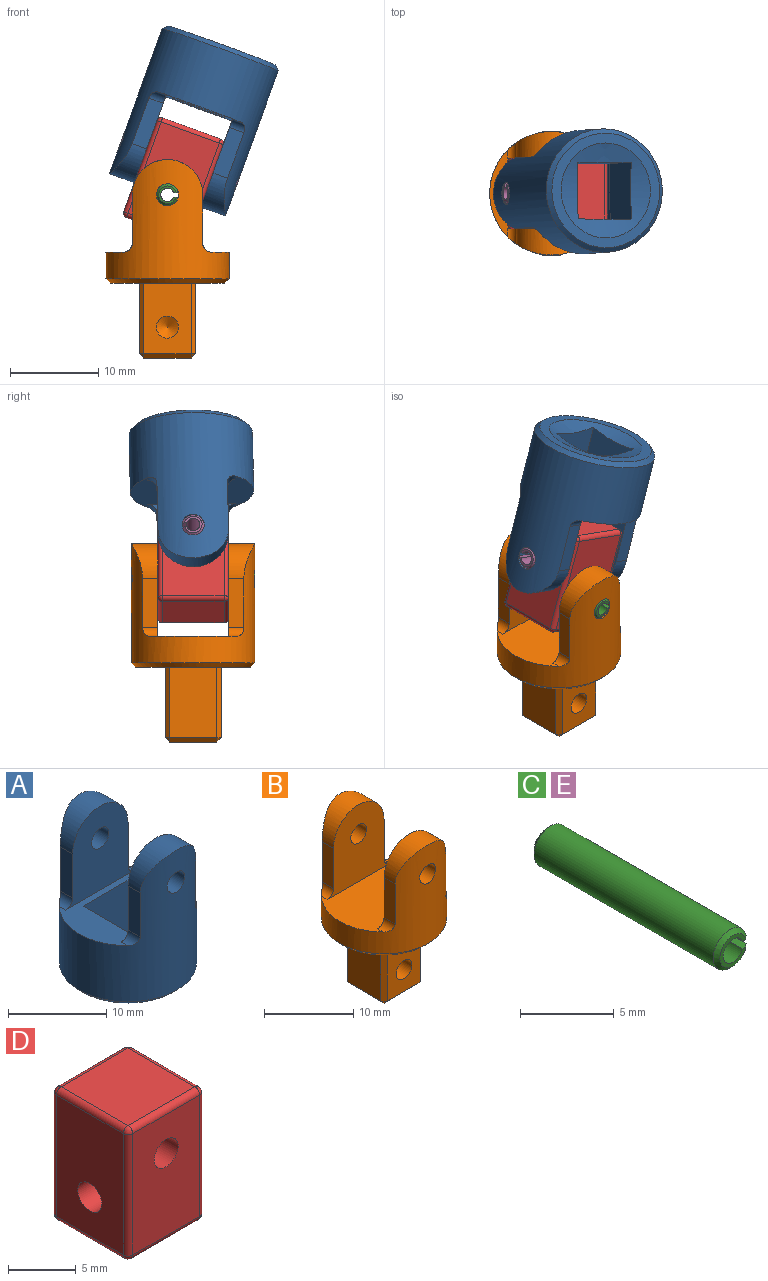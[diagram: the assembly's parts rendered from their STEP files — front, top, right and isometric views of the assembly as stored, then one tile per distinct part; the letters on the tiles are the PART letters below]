
ASSEMBLY  parts=5 mates=4
PART A: 23 faces, bbox 14x14x18 mm
  f0: plane 13x13mm, normal (0,0,-1), area 41.6mm2, adj f21,f22
  f1: plane 14x9.8mm, normal (0,0,1), area 65.4mm2, adj f3,f6,f8,f10,f13,f15,f16,f17
  f2: cylinder r=4mm len=8mm, axis (0,1,0), area 30mm2, adj f4,f5,f8,f16
  f3: cylinder r=1mm len=1.74mm, axis (0,1,0), area 2.3mm2, adj f1,f4,f8,f16
  f4: plane 5.5x1.74mm, normal (-1,0,0), area 9.6mm2, adj f2,f3,f8,f16
  f5: plane 5.5x1.74mm, normal (1,0,0), area 9.6mm2, adj f2,f6,f8,f16
  f6: cylinder r=1mm len=1.74mm, axis (0,1,0), area 2.3mm2, adj f1,f5,f8,f16
  f7: cylinder r=1.25mm len=3mm, axis (0,1,0), area 23.1mm2, adj f8,f16
  f8: cylinder r=7mm len=17.5mm, axis (0,0,-1), area 462.4mm2, adj f1,f2,f3,f4,f5,f6,f7,f9
  f9: cylinder r=4mm len=8mm, axis (0,1,0), area 30mm2, adj f8,f11,f12,f15
  f10: cylinder r=1mm len=1.74mm, axis (0,1,0), area 2.3mm2, adj f1,f8,f11,f15
  f11: plane 5.5x1.74mm, normal (-1,0,0), area 9.6mm2, adj f8,f9,f10,f15
  f12: plane 5.5x1.74mm, normal (1,0,0), area 9.6mm2, adj f8,f9,f13,f15
  f13: cylinder r=1mm len=1.74mm, axis (0,1,0), area 2.3mm2, adj f1,f8,f12,f15
  f14: cylinder r=1.25mm len=3mm, axis (0,1,0), area 23.1mm2, adj f8,f15
  f15: plane 10.5x10mm, normal (0,-1,0), area 72.7mm2, adj f1,f9,f10,f11,f12,f13,f14
  f16: plane 10.5x10mm, normal (0,1,0), area 72.7mm2, adj f1,f2,f3,f4,f5,f6,f7
  f17: plane 7.21x6.45mm, normal (-1,0,0), area 45mm2, adj f1,f18,f20,f22
  f18: plane 7.21x6.45mm, normal (0,-1,0), area 45mm2, adj f1,f17,f19,f22
  f19: plane 7.21x6.45mm, normal (1,0,0), area 45mm2, adj f1,f18,f20,f22
  f20: plane 7.21x6.45mm, normal (0,1,0), area 45mm2, adj f1,f17,f19,f22
  f21: cone r=7mm half-angle=45deg, axis (0,0,1), area 30mm2, adj f0,f8
  f22: sphere r=15mm, area 52mm2, adj f0,f17,f18,f19,f20
PART B: 37 faces, bbox 14x14x22.5 mm
  f0: cylinder r=4mm len=8mm, axis (0,1,0), area 30mm2, adj f2,f3,f6,f16
  f1: cylinder r=1mm len=1.74mm, axis (0,1,0), area 2.3mm2, adj f2,f6,f9,f16
  f2: plane 5.5x1.74mm, normal (-1,0,0), area 9.6mm2, adj f0,f1,f6,f16
  f3: plane 5.5x1.74mm, normal (1,0,0), area 9.6mm2, adj f0,f4,f6,f16
  f4: cylinder r=1mm len=1.74mm, axis (0,1,0), area 2.3mm2, adj f3,f6,f9,f16
  f5: cylinder r=1.25mm len=3mm, axis (0,1,0), area 23.1mm2, adj f6,f16
  f6: cylinder r=7mm len=14mm, axis (0,0,-1), area 286.4mm2, adj f0,f1,f2,f3,f4,f5,f8,f9
  f7: plane 13x13mm, normal (0,0,-1), area 92.9mm2, adj f17,f18,f19,f20,f22,f23,f25,f28
  f8: cylinder r=4mm len=8mm, axis (0,1,0), area 30mm2, adj f6,f11,f12,f15
  f9: plane 14x9.8mm, normal (0,0,1), area 107mm2, adj f1,f4,f6,f10,f13,f15,f16
  f10: cylinder r=1mm len=1.74mm, axis (0,1,0), area 2.3mm2, adj f6,f9,f11,f15
  f11: plane 5.5x1.74mm, normal (-1,0,0), area 9.6mm2, adj f6,f8,f10,f15
  f12: plane 5.5x1.74mm, normal (1,0,0), area 9.6mm2, adj f6,f8,f13,f15
  f13: cylinder r=1mm len=1.74mm, axis (0,1,0), area 2.3mm2, adj f6,f9,f12,f15
  f14: cylinder r=1.25mm len=3mm, axis (0,1,0), area 23.1mm2, adj f6,f15
  f15: plane 10.5x10mm, normal (0,-1,0), area 72.7mm2, adj f8,f9,f10,f11,f12,f13,f14
  f16: plane 10.5x10mm, normal (0,1,0), area 72.7mm2, adj f0,f1,f2,f3,f4,f5,f9
  f17: plane 8x5.35mm, normal (1,0,0), area 42.8mm2, adj f7,f28,f32,f34
  f18: plane 8x5.35mm, normal (0,1,0), area 42.8mm2, adj f7,f25,f31,f34
  f19: plane 8x5.35mm, normal (-1,0,0), area 42.8mm2, adj f7,f23,f25,f26
  f20: plane 8x5.35mm, normal (0,-1,0), area 37.9mm2, adj f7,f23,f27,f28,f35
  f21: plane 5.35x5.35mm, normal (0,0,-1), area 28.6mm2, adj f26,f27,f31,f32
  f22: cone r=7mm half-angle=45deg, axis (0,0,1), area 30mm2, adj f6,f7
  f23: plane 8x0.5mm, normal (-0.71,-0.71,0), area 5.7mm2, adj f7,f19,f20,f24
  f24: plane 0.5x0.5mm, normal (-0.58,-0.58,-0.58), area 0.2mm2, adj f23,f26,f27
  f25: plane 8x0.5mm, normal (-0.71,0.71,0), area 5.7mm2, adj f7,f18,f19,f29
  f26: plane 5.35x0.5mm, normal (-0.71,0,-0.71), area 3.8mm2, adj f19,f21,f24,f29
  f27: plane 5.35x0.5mm, normal (0,-0.71,-0.71), area 3.8mm2, adj f20,f21,f24,f30
  f28: plane 8x0.5mm, normal (0.71,-0.71,0), area 5.7mm2, adj f7,f17,f20,f30
  f29: plane 0.5x0.5mm, normal (-0.58,0.58,-0.58), area 0.2mm2, adj f25,f26,f31
  f30: plane 0.5x0.5mm, normal (0.58,-0.58,-0.58), area 0.2mm2, adj f27,f28,f32
  f31: plane 5.35x0.5mm, normal (0,0.71,-0.71), area 3.8mm2, adj f18,f21,f29,f33
  f32: plane 5.35x0.5mm, normal (0.71,0,-0.71), area 3.8mm2, adj f17,f21,f30,f33
  f33: plane 0.5x0.5mm, normal (0.58,0.58,-0.58), area 0.2mm2, adj f31,f32,f34
  f34: plane 8x0.5mm, normal (0.71,0.71,0), area 5.7mm2, adj f7,f17,f18,f33
  f35: cylinder r=1.25mm len=4mm, axis (0,-1,0), area 31.4mm2, adj f20,f36
  f36: cone r=0mm half-angle=59deg, axis (0,-1,0), area 5.7mm2, adj f35
PART C: 8 faces, bbox 2.5x14x2.5 mm
  f0: cylinder r=0.75mm len=14mm, axis (0,1,0), area 58.8mm2, adj f1,f3,f4,f5
  f1: plane 14.01x0.52mm, normal (0,0,-1), area 7.2mm2, adj f0,f2,f4,f5,f6,f7
  f2: cylinder r=1.25mm len=13.5mm, axis (0,1,0), area 99.2mm2, adj f1,f3,f6,f7
  f3: plane 14.01x0.52mm, normal (0,0,1), area 7.2mm2, adj f0,f2,f4,f5,f6,f7
  f4: plane 2x1.97mm, normal (0,-1,0), area 1.2mm2, adj f0,f1,f3,f7
  f5: plane 2x1.97mm, normal (0,1,0), area 1.2mm2, adj f0,f1,f3,f6
  f6: cone r=1.25mm half-angle=45deg, axis (0,-1,0), area 2.3mm2, adj f1,f2,f3,f5
  f7: cone r=1mm half-angle=45deg, axis (0,1,0), area 2.3mm2, adj f1,f2,f3,f4
PART D: 28 faces, bbox 8x8x12 mm
  f0: cylinder r=0.5mm len=11mm, axis (0,0,-1), area 8.6mm2, adj f1,f7,f15,f23
  f1: plane 11x7mm, normal (0,1,0), area 72.1mm2, adj f0,f2,f17,f25,f27
  f2: cylinder r=0.5mm len=11mm, axis (0,0,-1), area 8.6mm2, adj f1,f3,f16,f24
  f3: plane 11x7mm, normal (-1,0,0), area 72.1mm2, adj f2,f4,f14,f22,f26
  f4: cylinder r=0.5mm len=11mm, axis (0,0,-1), area 8.6mm2, adj f3,f5,f12,f20
  f5: plane 11x7mm, normal (0,-1,0), area 72.1mm2, adj f4,f6,f10,f18,f27
  f6: cylinder r=0.5mm len=11mm, axis (0,0,-1), area 8.6mm2, adj f5,f7,f11,f19
  f7: plane 11x7mm, normal (1,0,0), area 72.1mm2, adj f0,f6,f13,f21,f26
  f8: plane 7x7mm, normal (0,0,1), area 49mm2, adj f18,f21,f22,f25
  f9: plane 7x7mm, normal (0,0,-1), area 49mm2, adj f10,f13,f14,f17
  f10: cylinder r=0.5mm len=7mm, axis (1,0,0), area 5.5mm2, adj f5,f9,f11,f12
  f11: sphere r=0.5mm, area 0.4mm2, adj f6,f10,f13
  f12: sphere r=0.5mm, area 0.4mm2, adj f4,f10,f14
  f13: cylinder r=0.5mm len=7mm, axis (0,1,0), area 5.5mm2, adj f7,f9,f11,f15
  f14: cylinder r=0.5mm len=7mm, axis (0,-1,0), area 5.5mm2, adj f3,f9,f12,f16
  f15: sphere r=0.5mm, area 0.4mm2, adj f0,f13,f17
  f16: sphere r=0.5mm, area 0.4mm2, adj f2,f14,f17
  f17: cylinder r=0.5mm len=7mm, axis (-1,0,0), area 5.5mm2, adj f1,f9,f15,f16
  f18: cylinder r=0.5mm len=7mm, axis (-1,0,0), area 5.5mm2, adj f5,f8,f19,f20
  f19: sphere r=0.5mm, area 0.4mm2, adj f6,f18,f21
  f20: sphere r=0.5mm, area 0.4mm2, adj f4,f18,f22
  f21: cylinder r=0.5mm len=7mm, axis (0,-1,0), area 5.5mm2, adj f7,f8,f19,f23
  f22: cylinder r=0.5mm len=7mm, axis (0,1,0), area 5.5mm2, adj f3,f8,f20,f24
  f23: sphere r=0.5mm, area 0.4mm2, adj f0,f21,f25
  f24: sphere r=0.5mm, area 0.4mm2, adj f2,f22,f25
  f25: cylinder r=0.5mm len=7mm, axis (1,0,0), area 5.5mm2, adj f1,f8,f23,f24
  f26: cylinder r=1.25mm len=8mm, axis (1,0,0), area 62.8mm2, adj f3,f7
  f27: cylinder r=1.25mm len=8mm, axis (0,-1,0), area 62.8mm2, adj f1,f5
PART E: same geometry as C
PLACE A rot(axis=(-0.7,-0.7,0.13),166.7deg) t=(1.96,5.17,27.87)mm
PLACE B t=(-4.2,4.88,0.95)mm fixed
PLACE C t=(-4.2,11.88,10.95)mm
PLACE D rot(axis=(-0.17,0.17,-0.97),91.7deg) t=(-5.57,4.88,7.2)mm
PLACE E rot(axis=(-0.7,-0.7,0.13),166.7deg) t=(3.75,4.88,12.32)mm
MATE revolute E.f0 <-> D.f27  axis (0.94,0,-0.34) through (-2.83,4.88,14.71)mm
MATE fastened E.f0 <-> A.f7  axis (0.94,0,-0.34) through (-2.83,4.88,14.71)mm
MATE fastened C.f0 <-> B.f5  axis (0,1,0) through (-4.2,4.88,10.95)mm
MATE revolute D.f26 <-> B.f5  axis (0,-1,0) through (-4.2,4.88,10.95)mm
